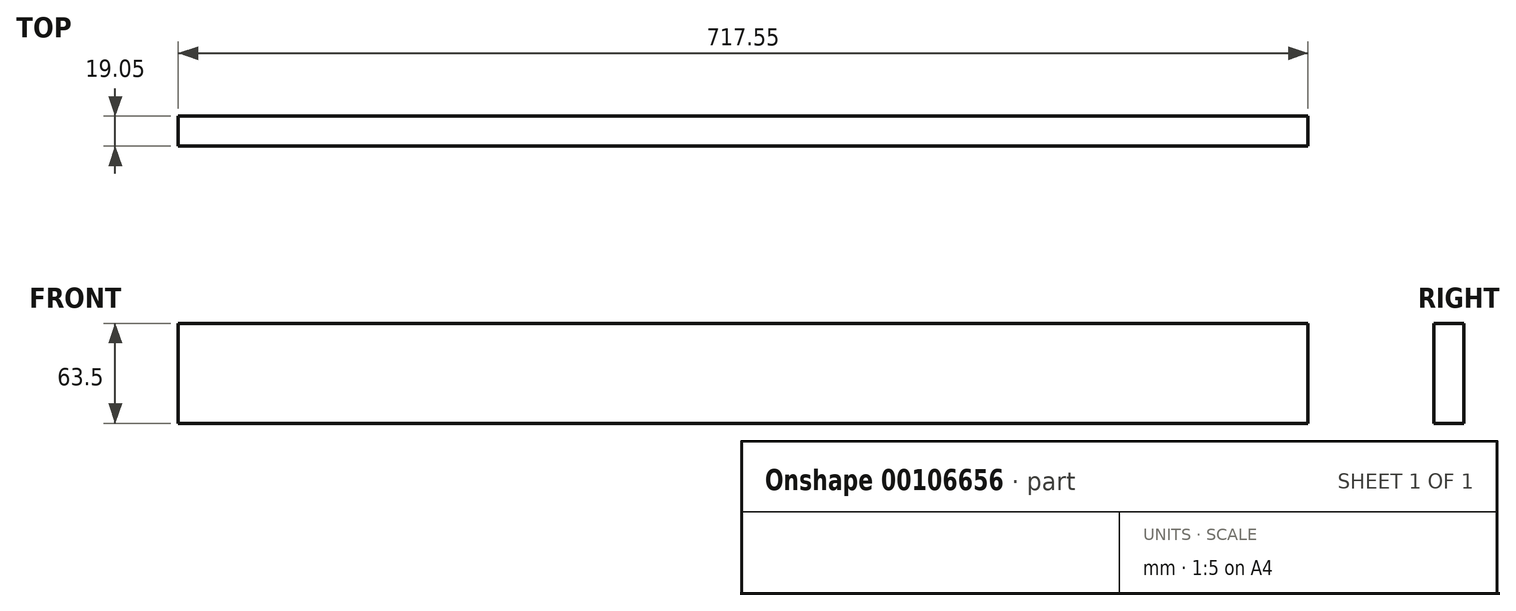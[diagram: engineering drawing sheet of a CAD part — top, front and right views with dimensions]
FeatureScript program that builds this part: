
annotation { "Feature Type Name" : "Feature", "Feature Type Description" : "" }
export const myFeature = defineFeature(function(context is Context, id is Id, definition is map)
    precondition{}
    {
        {
            var Q0;
            Q0=qCreatedBy(makeId("Front.planeOp"),FACE);
            var sketch = newSketch(context, id + "F0", { "sketchPlane" : qUnion([Q0])});
            skLineSegment(sketch, "E0.bottom", {"start": v(0, 0) * mm, "end": v(717.55, 0) * mm});
            skLineSegment(sketch, "E0.top", {"start": v(0, 63.5) * mm, "end": v(717.55, 63.5) * mm});
            skLineSegment(sketch, "E0.left", {"start": v(0, 0) * mm, "end": v(0, 63.5) * mm});
            skLineSegment(sketch, "E0.right", {"start": v(717.55, 0) * mm, "end": v(717.55, 63.5) * mm});
            skSolve(sketch);
        }
        {
            var Q0;
            Q0=makeQuery(id+"F0.imprint","IMPRINT",FACE,{"disambiguationData":[TD([[makeQuery(id+"F0.imprint","IMPRINT",EDGE,{"derivedFrom":sQuery(id+"F0.wireOp",EDGE,"E0.bottom")}),1.0]])]});
            extrude(context, id + "F1", {"entities" : qUnion([Q0]), "depth" : 19.05 * mm});
        }
    });
